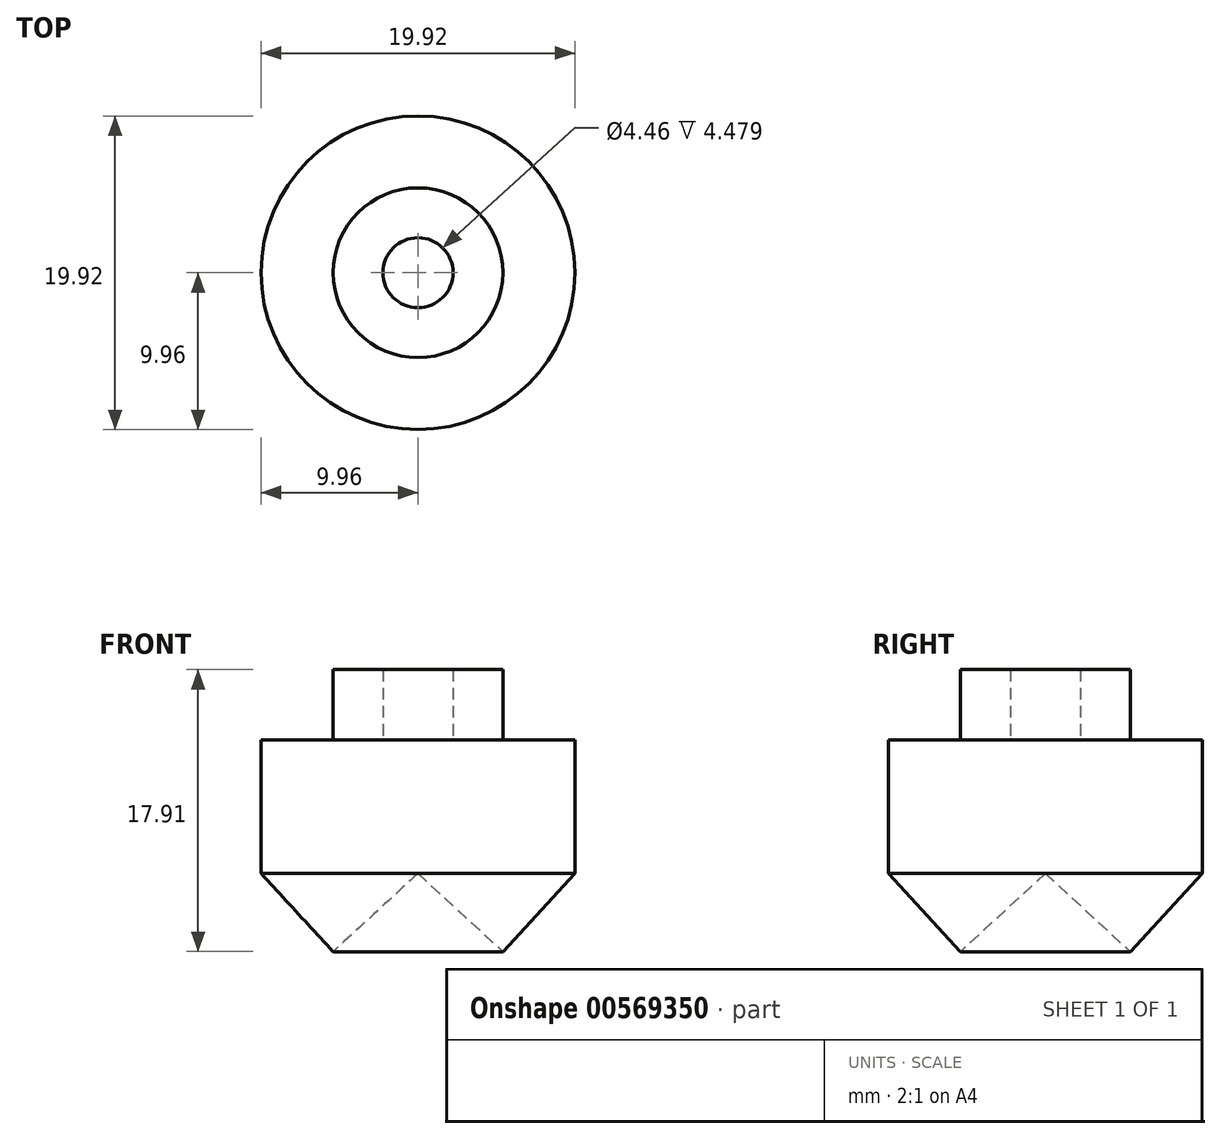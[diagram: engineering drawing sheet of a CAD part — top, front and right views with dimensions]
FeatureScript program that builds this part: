
annotation { "Feature Type Name" : "Feature", "Feature Type Description" : "" }
export const myFeature = defineFeature(function(context is Context, id is Id, definition is map)
    precondition{}
    {
        {
            var Q0;
            Q0=qCreatedBy(makeId("Front.planeOp"),FACE);
            var sketch = newSketch(context, id + "F0", { "sketchPlane" : qUnion([Q0])});
            skLineSegment(sketch, "E0", {"start": v(0, 0) * mm, "end": v(5.39, -4.96) * mm});
            skLineSegment(sketch, "E1", {"start": v(5.39, -4.96) * mm, "end": v(9.96, 0) * mm});
            skLineSegment(sketch, "E2", {"start": v(9.96, 0) * mm, "end": v(9.96, 8.47) * mm});
            skLineSegment(sketch, "E3", {"start": v(9.96, 8.47) * mm, "end": v(5.39, 8.47) * mm});
            skLineSegment(sketch, "E4", {"start": v(5.39, 8.47) * mm, "end": v(5.39, 12.95) * mm});
            skLineSegment(sketch, "E5", {"start": v(5.39, 12.95) * mm, "end": v(2.23, 12.95) * mm});
            skLineSegment(sketch, "E6", {"start": v(2.23, 12.95) * mm, "end": v(2.23, 8.47) * mm});
            skLineSegment(sketch, "E7", {"start": v(0, 0) * mm, "end": v(0, 8.47) * mm});
            skLineSegment(sketch, "E8", {"start": v(0, 8.47) * mm, "end": v(2.23, 8.47) * mm});
            skSolve(sketch);
        }
        {
            var Q0;
            Q0=makeQuery(id+"F0.imprint","IMPRINT",FACE,{"disambiguationData":[TD([[makeQuery(id+"F0.imprint","IMPRINT",EDGE,{"derivedFrom":sQuery(id+"F0.wireOp",EDGE,"E0")}),1.0]])]});
            var Q1;
            Q1=sQuery(id+"F0.wireOp",EDGE,"E7");
            revolve(context, id + "F1", {"entities" : qUnion([Q0]), "axis" : qUnion([Q1]), "revolveType" : RevolveType.FULL});
        }
    });
